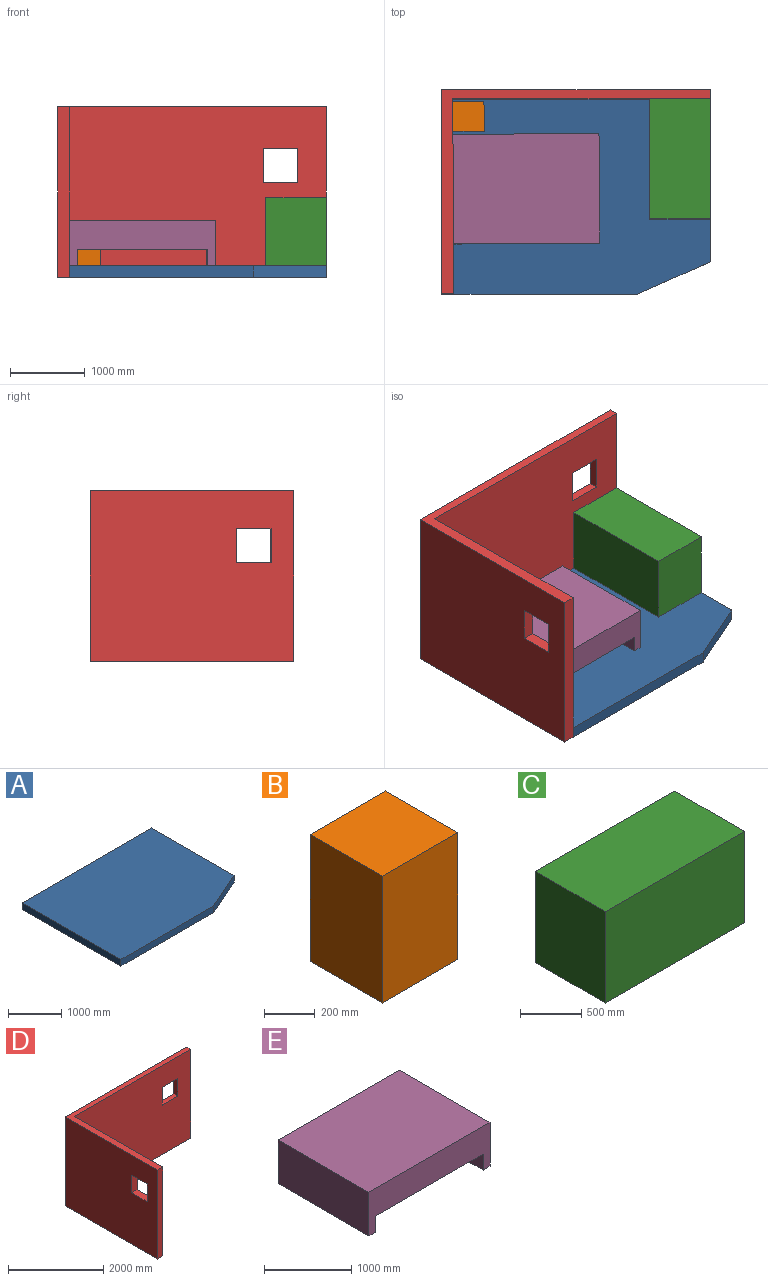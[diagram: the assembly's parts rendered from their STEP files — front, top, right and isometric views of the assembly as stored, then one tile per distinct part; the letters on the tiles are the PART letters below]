
ASSEMBLY  parts=5 mates=11
PART A: 7 faces, bbox 3454.4x2616.1x152.4 mm
  f0: plane 3454.4x152.4mm, normal (0,1,0), area 526450.6mm2, adj f1,f4,f5,f6
  f1: plane 2616.15x152.4mm, normal (-1,-0.01,0), area 398708.9mm2, adj f0,f2,f5,f6
  f2: plane 2463.8x152.4mm, normal (0,-1,0), area 375483.1mm2, adj f1,f3,f5,f6
  f3: plane 974.2x431.75mm, normal (0.41,-0.91,0), area 162394.9mm2, adj f2,f4,f5,f6
  f4: plane 2184.4x152.4mm, normal (1,0,0), area 332902.6mm2, adj f0,f3,f5,f6
  f5: plane 3454.4x2616.15mm, normal (0,0,1), area 8805464.3mm2, adj f0,f1,f2,f3,f4
  f6: plane 3454.4x2616.15mm, normal (0,0,-1), area 8805464.3mm2, adj f0,f1,f2,f3,f4
PART B: 6 faces, bbox 419.1x400.1x609.6 mm
  f0: plane 609.6x419.1mm, normal (0,1,0), area 255483.4mm2, adj f1,f3,f4,f5
  f1: plane 609.6x400.05mm, normal (-1,0,0), area 243870.5mm2, adj f0,f2,f4,f5
  f2: plane 609.6x419.1mm, normal (0,-1,0), area 255483.4mm2, adj f1,f3,f4,f5
  f3: plane 609.6x400.05mm, normal (1,0,0), area 243870.5mm2, adj f0,f2,f4,f5
  f4: plane 419.1x400.05mm, normal (0,0,1), area 167661mm2, adj f0,f1,f2,f3
  f5: plane 419.1x400.05mm, normal (0,0,-1), area 167661mm2, adj f0,f1,f2,f3
PART C: 6 faces, bbox 1609.7x809.6x914.4 mm
  f0: plane 1609.73x914.4mm, normal (0,1,0), area 1471932.5mm2, adj f1,f3,f4,f5
  f1: plane 914.4x809.63mm, normal (-1,0,0), area 740321.1mm2, adj f0,f2,f4,f5
  f2: plane 1609.73x914.4mm, normal (0,-1,0), area 1471932.5mm2, adj f1,f3,f4,f5
  f3: plane 914.4x809.63mm, normal (1,0,0), area 740321.1mm2, adj f0,f2,f4,f5
  f4: plane 1609.73x809.63mm, normal (0,0,1), area 1303273.6mm2, adj f0,f1,f2,f3
  f5: plane 1609.73x809.63mm, normal (0,0,-1), area 1303273.6mm2, adj f0,f1,f2,f3
PART D: 16 faces, bbox 3601.6x2734.4x2286 mm
  f0: plane 3454.4x2286mm, normal (0,-1,0), area 7687726.6mm2, adj f2,f4,f6,f7,f12,f13,f14,f15
  f1: plane 3601.56x2286mm, normal (0,1,0), area 8024126.1mm2, adj f3,f4,f6,f7,f12,f13,f14,f15
  f2: plane 2616.15x2286mm, normal (1,0.01,0), area 5771601.4mm2, adj f0,f5,f6,f7,f8,f9,f10,f11
  f3: plane 2734.36x2286mm, normal (-1,0,0), area 6041700.3mm2, adj f1,f5,f6,f7,f8,f9,f10,f11
  f4: plane 2286x118.21mm, normal (1,0,0), area 270220.6mm2, adj f0,f1,f6,f7
  f5: plane 2286x163.56mm, normal (0,-1,0), area 373894.6mm2, adj f2,f3,f6,f7
  f6: plane 3601.56x2734.36mm, normal (0,0,1), area 832166.4mm2, adj f0,f1,f2,f3,f4,f5
  f7: plane 3601.56x2734.36mm, normal (0,0,-1), area 832166.4mm2, adj f0,f1,f2,f3,f4,f5
  f8: plane 458.2x161.62mm, normal (0,0,-1), area 73240.7mm2, adj f2,f3,f9,f11
  f9: plane 457.2x161.62mm, normal (-0.01,1,0), area 73896mm2, adj f2,f3,f8,f10
  f10: plane 458.2x161.62mm, normal (0,0,1), area 73240.7mm2, adj f2,f3,f9,f11
  f11: plane 457.2x158.76mm, normal (0.01,-1,0), area 72585.4mm2, adj f2,f3,f8,f10
  f12: plane 457.2x118.21mm, normal (0,0,-1), area 54044.1mm2, adj f0,f1,f13,f15
  f13: plane 457.2x118.21mm, normal (1,0,0), area 54044.1mm2, adj f0,f1,f12,f14
  f14: plane 457.2x118.21mm, normal (0,0,1), area 54044.1mm2, adj f0,f1,f13,f15
  f15: plane 457.2x118.21mm, normal (-1,0,0), area 54044.1mm2, adj f0,f1,f12,f14
PART E: 10 faces, bbox 1959x1470x609.6 mm
  f0: plane 1470.03x112.18mm, normal (0,0,-1), area 164912.7mm2, adj f1,f3,f4,f8
  f1: plane 1958.98x609.6mm, normal (0,1,0), area 803937.6mm2, adj f0,f2,f4,f5,f6,f7,f8,f9
  f2: plane 1470.03x609.6mm, normal (-1,0,0), area 896127.2mm2, adj f1,f3,f5,f6
  f3: plane 1958.98x609.6mm, normal (0,-1,0), area 803937.6mm2, adj f0,f2,f4,f5,f6,f7,f8,f9
  f4: plane 1470.03x609.6mm, normal (1,0,0), area 896127.2mm2, adj f0,f1,f3,f5
  f5: plane 1958.98x1470.03mm, normal (0,0,1), area 2879742.2mm2, adj f1,f2,f3,f4
  f6: plane 1470.03x106.89mm, normal (0,0,-1), area 157133mm2, adj f1,f2,f3,f7
  f7: plane 1470.03x224.3mm, normal (1,0,0), area 329721.5mm2, adj f1,f3,f6,f9
  f8: plane 1470.03x224.3mm, normal (-1,0,0), area 329721.5mm2, adj f0,f1,f3,f9
  f9: plane 1739.9x1470.03mm, normal (0,0,-1), area 2557696.5mm2, adj f1,f3,f7,f8
PLACE A t=(1932.76,-601.32,-1175.4)mm
PLACE B rot(axis=(0,0,1),0.4deg) t=(428.08,102.51,-1023)mm
PLACE C rot(axis=(0,0,-1),90deg) t=(3135.73,-472.18,-1023)mm
PLACE D t=(1932.76,-601.32,-1175.4)mm
PLACE E rot(axis=(0,0,1),0.4deg) t=(1201.11,-1193.55,-1023)mm
MATE planar A.f5 <-> E.f6  axis (0,0,1) through (1915.39,-937.54,-1023)mm
MATE planar C.f5 <-> A.f5  axis (0,0,-1) through (3671.89,-463.19,-1023)mm
MATE planar C.f0 <-> D.f4  axis (1,0,0) through (3671.89,-463.19,-565.8)mm
MATE planar A.f6 <-> D.f7  axis (0,0,-1) through (1915.39,-937.54,-1175.4)mm
MATE planar A.f0 <-> D.f0  axis (0,1,0) through (1944.69,341.67,-1099.2)mm
MATE parallel C.f3 <-> D.f0  axis (0,-1,0) through (3671.89,-1268.05,-565.8)mm
MATE planar C.f1 <-> D.f0  axis (0,1,0) through (3267.07,341.67,-108.6)mm
MATE planar E.f2 <-> D.f2  axis (-1,-0.01,0) through (229.69,-1603.86,-718.2)mm
MATE planar A.f4 <-> D.f4  axis (1,0,0) through (3671.89,-750.53,-1099.2)mm
MATE planar B.f5 <-> A.f5  axis (0,0,-1) through (428.5,108.97,-1023)mm
MATE planar B.f1 <-> D.f2  axis (-1,-0.01,0) through (218.95,107.66,-718.2)mm
